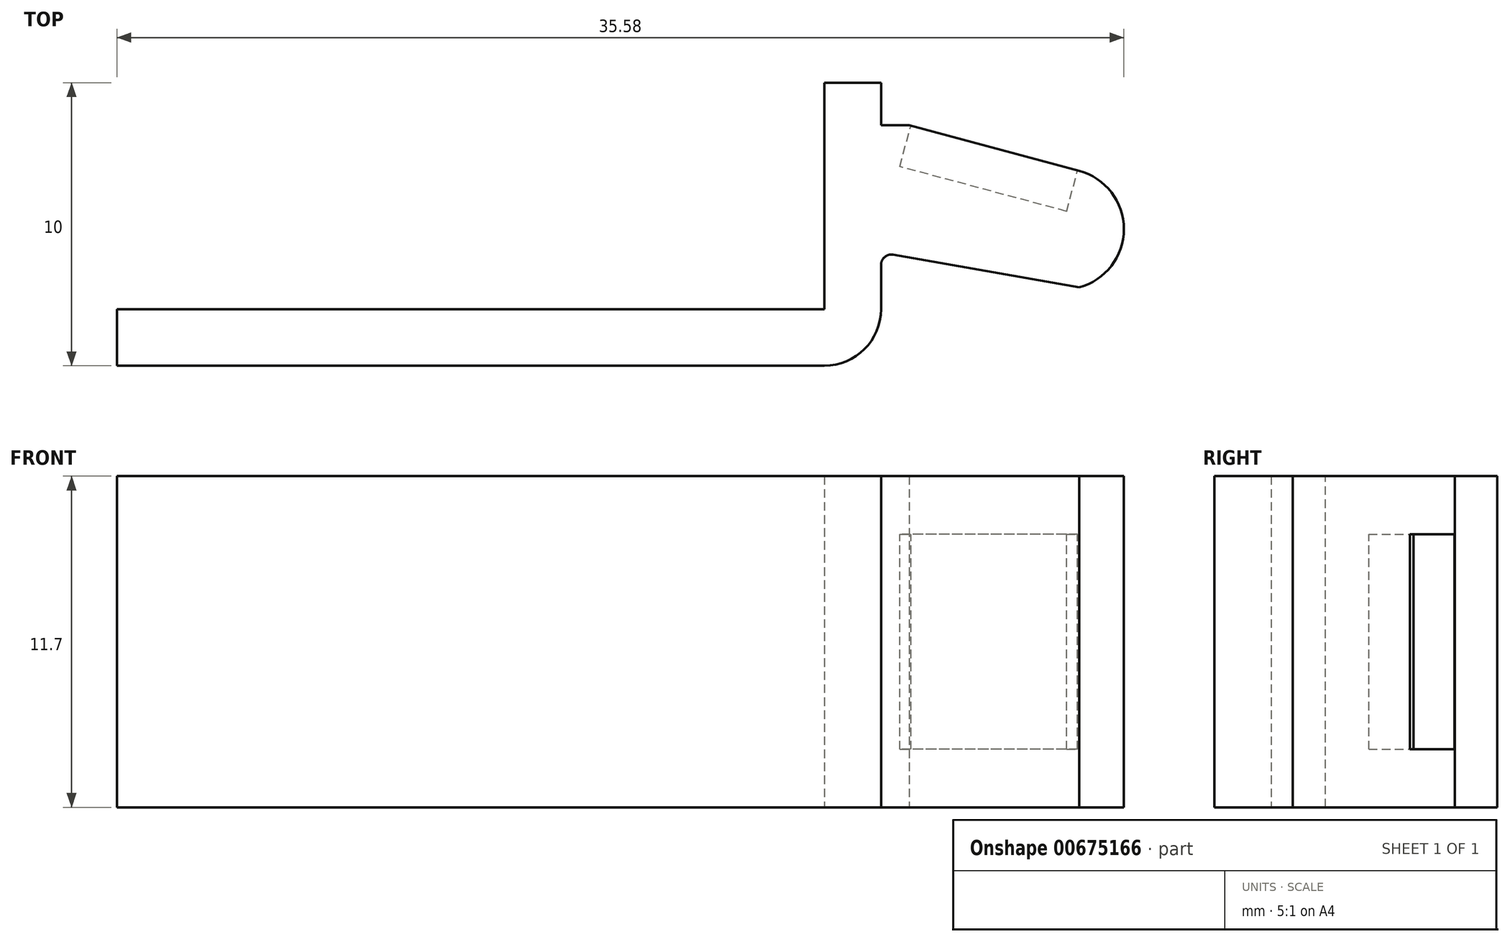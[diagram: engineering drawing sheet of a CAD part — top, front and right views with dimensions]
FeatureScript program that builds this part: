
annotation { "Feature Type Name" : "Feature", "Feature Type Description" : "" }
export const myFeature = defineFeature(function(context is Context, id is Id, definition is map)
    precondition{}
    {
        {
            var Q0;
            Q0=qCreatedBy(makeId("Top.planeOp"),FACE);
            var sketch = newSketch(context, id + "F0", { "sketchPlane" : qUnion([Q0])});
            skLineSegment(sketch, "E0", {"start": v(0, 1) * mm, "end": v(0, -1) * mm});
            skLineSegment(sketch, "E1", {"start": v(0, 1) * mm, "end": v(25, 1) * mm});
            skLineSegment(sketch, "E2", {"start": v(25, 1) * mm, "end": v(25, 9) * mm});
            skLineSegment(sketch, "E3", {"start": v(25, 9) * mm, "end": v(27, 9) * mm});
            skLineSegment(sketch, "E4", {"start": v(27, 9) * mm, "end": v(27, 7.5) * mm});
            skLineSegment(sketch, "E5", {"start": v(27, 7.5) * mm, "end": v(28, 7.5) * mm});
            skLineSegment(sketch, "E6", {"start": v(0, -1) * mm, "end": v(27, -1) * mm});
            skPoint(sketch, "E7.visualSharp", {"position": v(27, 3) * mm});
            skLineSegment(sketch, "E8", {"start": v(27, -1) * mm, "end": v(27, 3) * mm});
            skPoint(sketch, "E9.start.orphan", {"position": v(34, 3) * mm});
            skPoint(sketch, "E10.end.orphan", {"position": v(34, 6.79) * mm});
            skLineSegment(sketch, "E11", {"start": v(28, 7.5) * mm, "end": v(34, 5.9) * mm});
            skLineSegment(sketch, "E12", {"start": v(27, 3) * mm, "end": v(34, 1.77) * mm});
            skArc(sketch, "E13", {"start": v(34, 1.77) * mm, "mid": v(35.58, 3.83) * mm, "end": v(34, 5.9) * mm});
            skSolve(sketch);
        }
        {
            var Q0;
            Q0 = qSketchRegion(id + "F0", true);
            extrude(context, id + "F1", {"entities" : qUnion([Q0]), "endBound" : BoundingType.SYMMETRIC, "depth" : 11.7 * mm, "offsetDistance" : 25 * mm});
        }
        {
            var Q0;
            Q0=makeQuery(id+"F1.opExtrude","SWEPT_EDGE",EDGE,{"disambiguationData":[OSD([sQuery(id+"F0.wireOp",EDGE,"E6"),sQuery(id+"F0.wireOp",EDGE,"E8")])]});
            fillet(context, id + "F2", {"entities" : qUnion([Q0]), "radius" : 2 * mm, "tangentPropagation" : true, "allowEdgeOverflow" : false});
        }
        {
            var Q0;
            Q0=makeQuery(id+"F1.opExtrude","SWEPT_EDGE",EDGE,{"disambiguationData":[OSD([sQuery(id+"F0.wireOp",EDGE,"E8"),sQuery(id+"F0.wireOp",EDGE,"E12")])]});
            fillet(context, id + "F3", {"entities" : qUnion([Q0]), "radius" : 0.37 * mm, "tangentPropagation" : true, "allowEdgeOverflow" : false});
        }
        {
            var Q0;
            Q0=makeQuery(id+"F1.opExtrude","SWEPT_FACE",FACE,{"disambiguationData":[OSD([sQuery(id+"F0.wireOp",EDGE,"E11")])]});
            var sketch = newSketch(context, id + "F4", { "sketchPlane" : qUnion([Q0])});
            skLineSegment(sketch, "E14", {"start": v(-31.32, 0) * mm, "end": v(-25.1, 0) * mm, "construction": true});
            skLineSegment(sketch, "E15", {"start": v(-28.21, 5.85) * mm, "end": v(-28.21, -5.85) * mm, "construction": true});
            skLineSegment(sketch, "E16.bottom", {"start": v(-31.26, -3.8) * mm, "end": v(-25.16, -3.8) * mm});
            skLineSegment(sketch, "E16.top", {"start": v(-31.26, 3.8) * mm, "end": v(-25.16, 3.8) * mm});
            skLineSegment(sketch, "E16.left", {"start": v(-31.26, -3.8) * mm, "end": v(-31.26, 3.8) * mm});
            skLineSegment(sketch, "E16.right", {"start": v(-25.16, -3.8) * mm, "end": v(-25.16, 3.8) * mm});
            skPoint(sketch, "E16.middle", {"position": v(-28.21, 0) * mm});
            skSolve(sketch);
        }
        {
            var Q0;
            Q0 = qSketchRegion(id + "F4", true);
            extrude(context, id + "F5", {"entities" : qUnion([Q0]), "operationType" : NewBodyOperationType.REMOVE, "oppositeDirection" : true, "depth" : 1.5 * mm, "offsetDistance" : 25 * mm});
        }
    });
